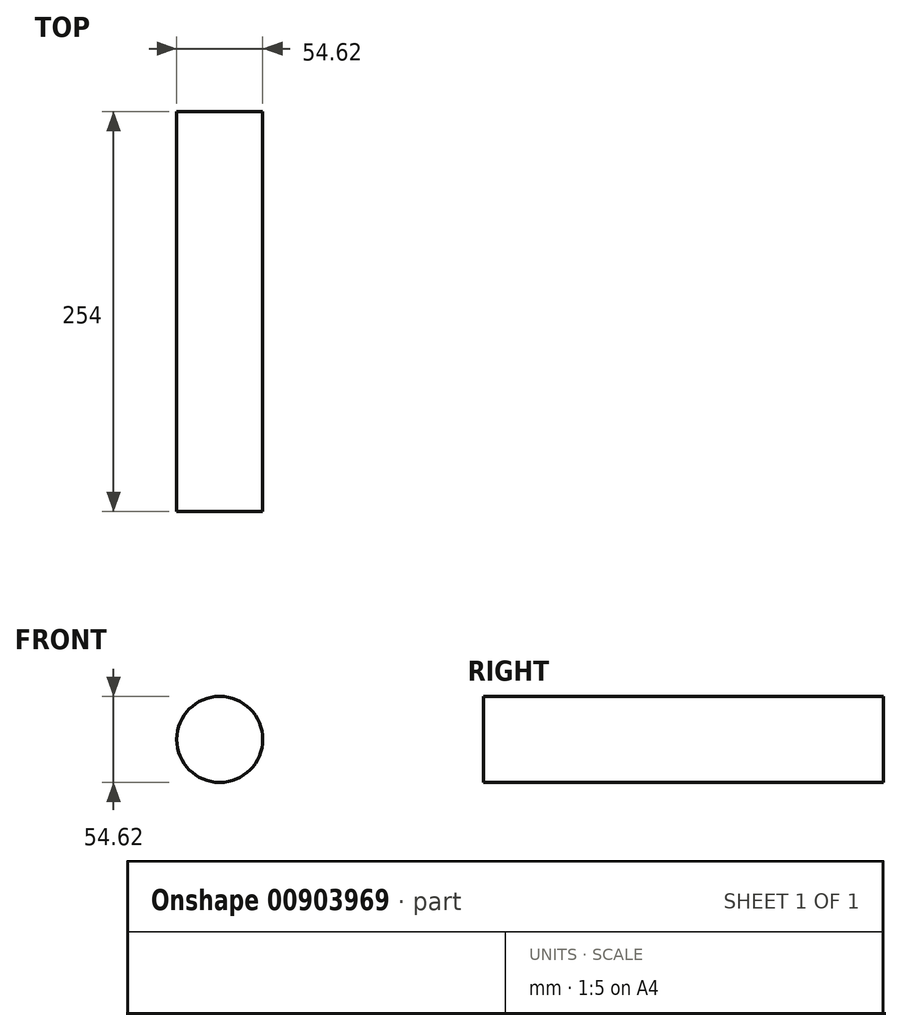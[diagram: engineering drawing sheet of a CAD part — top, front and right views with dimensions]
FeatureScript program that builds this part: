
annotation { "Feature Type Name" : "Feature", "Feature Type Description" : "" }
export const myFeature = defineFeature(function(context is Context, id is Id, definition is map)
    precondition{}
    {
        {
            var Q0;
            Q0=qCreatedBy(makeId("Front.planeOp"),FACE);
            var sketch = newSketch(context, id + "F0", { "sketchPlane" : qUnion([Q0])});
            skCircle(sketch, "E0", {"center": v(0, 0) * mm, "radius": 27.3 * mm});
            skSolve(sketch);
        }
        {
            var Q0;
            Q0 = qSketchRegion(id + "F0", true);
            extrude(context, id + "F1", {"entities" : qUnion([Q0]), "depth" : 254 * mm, "offsetDistance" : 25.4 * mm});
        }
    });
